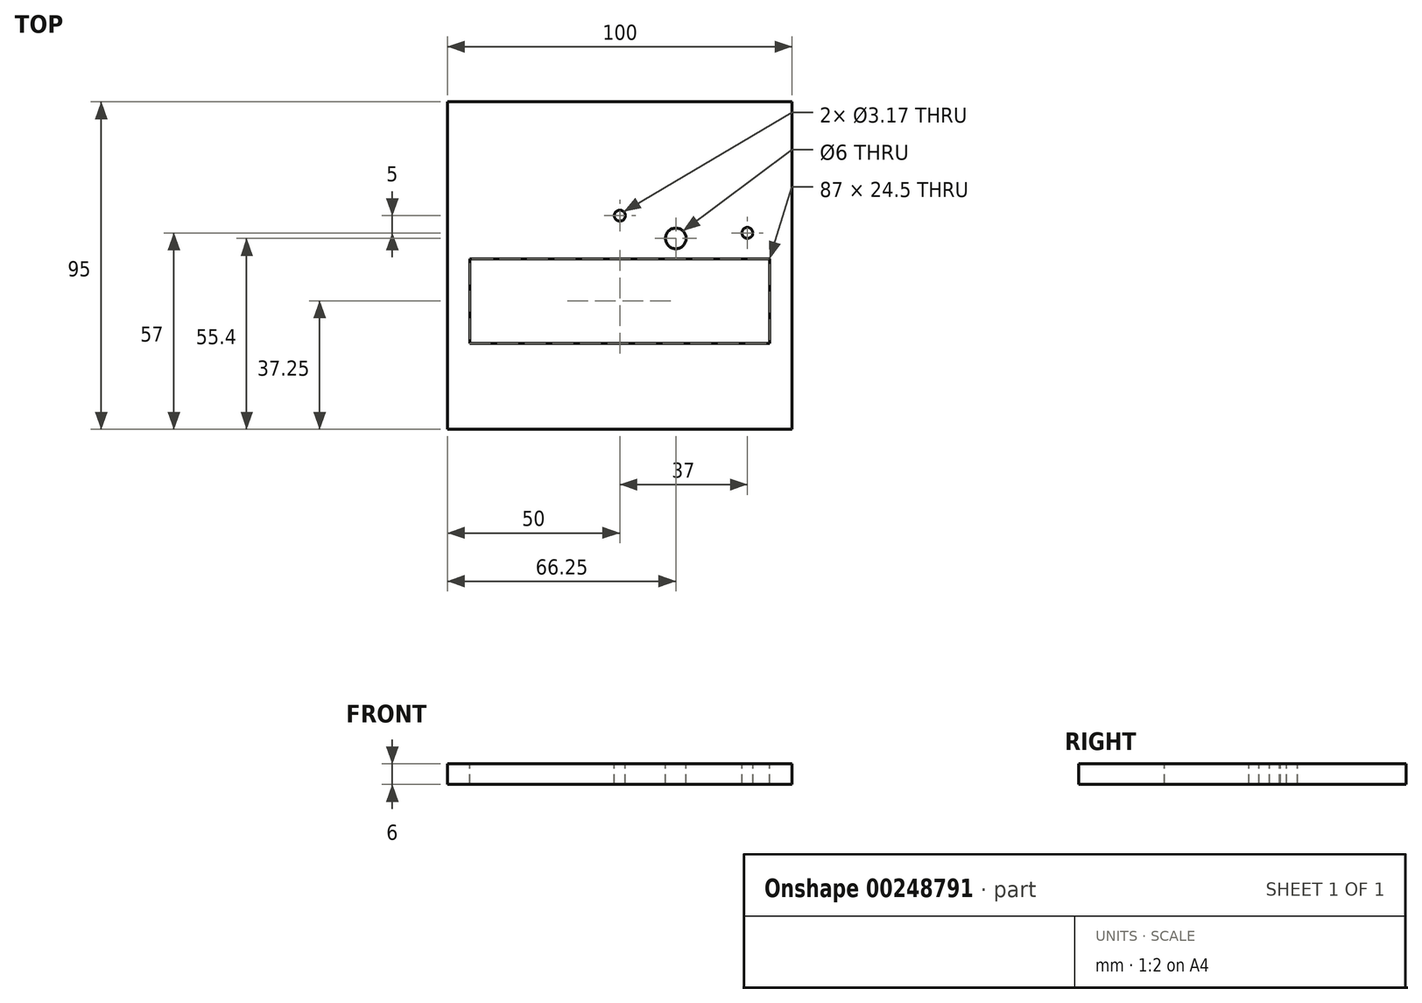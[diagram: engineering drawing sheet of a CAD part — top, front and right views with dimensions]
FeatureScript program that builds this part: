
annotation { "Feature Type Name" : "Feature", "Feature Type Description" : "" }
export const myFeature = defineFeature(function(context is Context, id is Id, definition is map)
    precondition{}
    {
        {
            var Q0;
            Q0=qCreatedBy(makeId("Top.planeOp"),FACE);
            var sketch = newSketch(context, id + "F0", { "sketchPlane" : qUnion([Q0])});
            skLineSegment(sketch, "E0.bottom", {"start": v(-50, 47.5) * mm, "end": v(50, 47.5) * mm});
            skLineSegment(sketch, "E0.top", {"start": v(-50, -47.5) * mm, "end": v(50, -47.5) * mm});
            skLineSegment(sketch, "E0.left", {"start": v(-50, 47.5) * mm, "end": v(-50, -47.5) * mm});
            skLineSegment(sketch, "E0.right", {"start": v(50, 47.5) * mm, "end": v(50, -47.5) * mm});
            skPoint(sketch, "E0.middle", {"position": v(0, 0) * mm});
            skSolve(sketch);
        }
        {
            var Q0;
            Q0=qCreatedBy(makeId("Top.planeOp"),FACE);
            var sketch = newSketch(context, id + "F1", { "sketchPlane" : qUnion([Q0])});
            skLineSegment(sketch, "E1.bottom", {"start": v(43.5, -22.5) * mm, "end": v(-43.5, -22.5) * mm});
            skLineSegment(sketch, "E1.top", {"start": v(43.5, 2) * mm, "end": v(-43.5, 2) * mm});
            skLineSegment(sketch, "E1.left", {"start": v(43.5, -22.5) * mm, "end": v(43.5, 2) * mm});
            skLineSegment(sketch, "E1.right", {"start": v(-43.5, -22.5) * mm, "end": v(-43.5, 2) * mm});
            skPoint(sketch, "E1.middle", {"position": v(0, -10.25) * mm});
            skSolve(sketch);
        }
        {
            var Q0;
            Q0=qCreatedBy(makeId("Top.planeOp"),FACE);
            var sketch = newSketch(context, id + "F2", { "sketchPlane" : qUnion([Q0])});
            skPoint(sketch, "E2", {"position": v(0, 9.5) * mm});
            skLineSegment(sketch, "E3", {"start": v(-1.05, 9.5) * mm, "end": v(0, 9.5) * mm, "construction": true});
            skLineSegment(sketch, "E4", {"start": v(0, 9.5) * mm, "end": v(0, 10.85) * mm, "construction": true});
            skCircle(sketch, "E5", {"center": v(0, 14.5) * mm, "radius": 1.59 * mm});
            skCircle(sketch, "E6", {"center": v(37, 9.5) * mm, "radius": 1.59 * mm});
            skCircle(sketch, "E7", {"center": v(16.25, 7.9) * mm, "radius": 3 * mm});
            skCircle(sketch, "E8.MirrorC", {"center": v(-37, 9.5) * mm, "radius": 1.59 * mm});
            skCircle(sketch, "E9.MirrorC", {"center": v(-16.25, 7.9) * mm, "radius": 3 * mm});
            skCircle(sketch, "E10.MirrorC", {"center": v(0, 4.5) * mm, "radius": 1.59 * mm});
            skSolve(sketch);
        }
        {
            var Q0;
            Q0=makeQuery(id+"F0.imprint","IMPRINT",FACE,{"disambiguationData":[TD([[makeQuery(id+"F0.imprint","IMPRINT",EDGE,{"derivedFrom":sQuery(id+"F0.wireOp",EDGE,"E0.bottom")}),-1.0]])]});
            extrude(context, id + "F3", {"entities" : qUnion([Q0]), "oppositeDirection" : true, "depth" : 6 * mm, "offsetDistance" : 25 * mm});
        }
        {
            var Q0;
            Q0=makeQuery(id+"F1.imprint","IMPRINT",FACE,{"disambiguationData":[TD([[makeQuery(id+"F1.imprint","IMPRINT",EDGE,{"derivedFrom":sQuery(id+"F1.wireOp",EDGE,"E1.bottom")}),-1.0]])]});
            var Q1;
            Q1=makeQuery(id+"F2.imprint","IMPRINT",FACE,{"disambiguationData":[TD([[makeQuery(id+"F2.imprint","IMPRINT",EDGE,{"derivedFrom":sQuery(id+"F2.wireOp",EDGE,"E8.MirrorC")}),-1.0]])]});
            var Q2;
            Q2=makeQuery(id+"F2.imprint","IMPRINT",FACE,{"disambiguationData":[TD([[makeQuery(id+"F2.imprint","IMPRINT",EDGE,{"derivedFrom":sQuery(id+"F2.wireOp",EDGE,"E9.MirrorC")}),-1.0]])]});
            var Q3;
            Q3=makeQuery(id+"F2.imprint","IMPRINT",FACE,{"disambiguationData":[TD([[makeQuery(id+"F2.imprint","IMPRINT",EDGE,{"derivedFrom":sQuery(id+"F2.wireOp",EDGE,"E10.MirrorC")}),-1.0]])]});
            var Q4;
            Q4=makeQuery(id+"F2.imprint","IMPRINT",FACE,{"disambiguationData":[TD([[makeQuery(id+"F2.imprint","IMPRINT",EDGE,{"derivedFrom":sQuery(id+"F2.wireOp",EDGE,"E5")}),1.0]])]});
            var Q5;
            Q5=makeQuery(id+"F2.imprint","IMPRINT",FACE,{"disambiguationData":[TD([[makeQuery(id+"F2.imprint","IMPRINT",EDGE,{"derivedFrom":sQuery(id+"F2.wireOp",EDGE,"E7")}),1.0]])]});
            var Q6;
            Q6=makeQuery(id+"F2.imprint","IMPRINT",FACE,{"disambiguationData":[TD([[makeQuery(id+"F2.imprint","IMPRINT",EDGE,{"derivedFrom":sQuery(id+"F2.wireOp",EDGE,"E6")}),1.0]])]});
            extrude(context, id + "F4", {"entities" : qUnion([Q0, Q1, Q2, Q3, Q4, Q5, Q6]), "operationType" : NewBodyOperationType.REMOVE, "oppositeDirection" : true, "depth" : 25 * mm, "offsetDistance" : 25 * mm});
        }
    });
